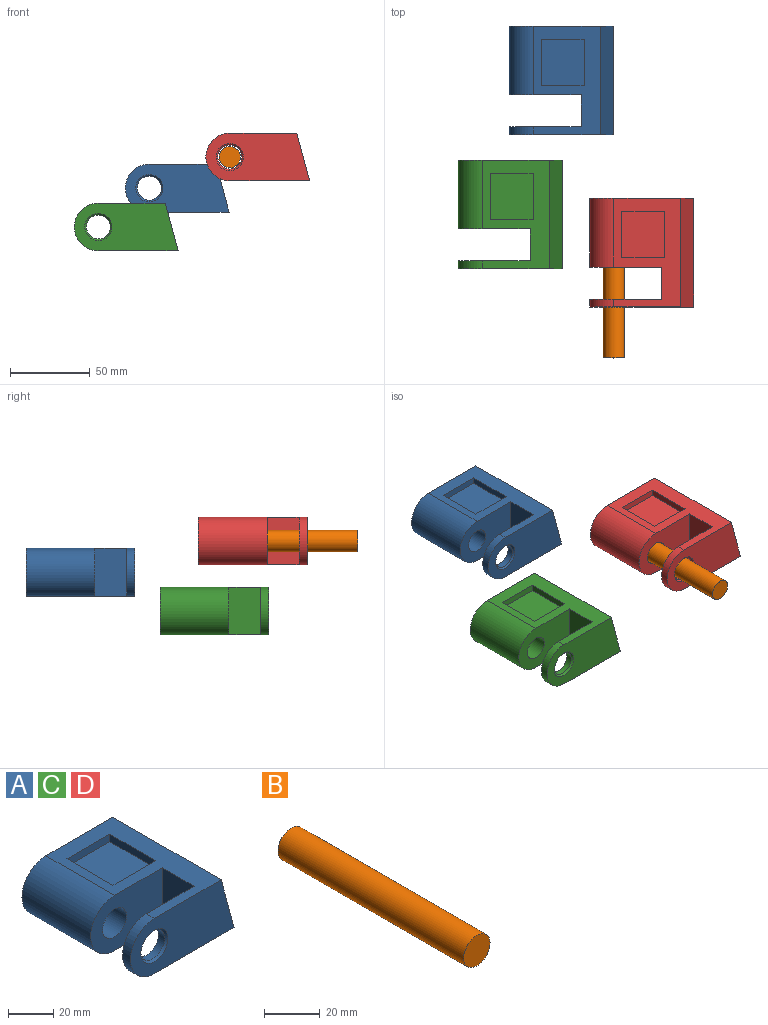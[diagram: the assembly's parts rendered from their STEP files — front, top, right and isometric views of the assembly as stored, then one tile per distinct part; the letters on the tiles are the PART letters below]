
ASSEMBLY  parts=4 mates=1
PART A: 19 faces, bbox 65x68.1x30 mm
  f0: plane 68.1x41.96mm, normal (0,0,1), area 1483.2mm2, adj f1,f2,f3,f5,f6,f7,f8,f9
  f1: cylinder r=15mm len=43.1mm, axis (0,1,0), area 2031mm2, adj f0,f4,f6,f9
  f2: plane 68.1x30mm, normal (0.97,0,0.26), area 2115.1mm2, adj f0,f4,f5,f6
  f3: cylinder r=15mm len=30mm, axis (0,1,0), area 235.6mm2, adj f0,f4,f5,f7
  f4: plane 68.1x50mm, normal (0,0,-1), area 2805mm2, adj f1,f2,f3,f5,f6,f7,f8,f9
  f5: plane 65x30mm, normal (0,-1,0), area 1505.9mm2, adj f0,f2,f3,f4,f12
  f6: plane 65x30mm, normal (0,1,0), area 1505.9mm2, adj f0,f1,f2,f4,f13
  f7: plane 45x30mm, normal (0,1,0), area 1076.7mm2, adj f0,f3,f4,f8,f11
  f8: plane 30x20mm, normal (-1,0,0), area 600mm2, adj f0,f4,f7,f9
  f9: plane 45x30mm, normal (0,-1,0), area 1076.7mm2, adj f0,f1,f4,f8,f10
  f10: cylinder r=7.5mm len=42.1mm, axis (0,1,0), area 1983.9mm2, adj f9,f13
  f11: cylinder r=7.5mm len=15mm, axis (0,1,0), area 188.5mm2, adj f7,f12
  f12: cone r=7.5mm half-angle=45deg, axis (0,-1,0), area 71.1mm2, adj f5,f11
  f13: cone r=7.5mm half-angle=45deg, axis (0,1,0), area 71.1mm2, adj f6,f10
  f14: plane 26.82x4.1mm, normal (0,1,0), area 110mm2, adj f0,f15,f17,f18
  f15: plane 28.87x4.1mm, normal (-1,0,0), area 118.4mm2, adj f0,f14,f16,f18
  f16: plane 26.82x4.1mm, normal (0,-1,0), area 110mm2, adj f0,f15,f17,f18
  f17: plane 28.87x4.1mm, normal (1,0,0), area 118.4mm2, adj f0,f14,f16,f18
  f18: plane 28.87x26.82mm, normal (0,0,1), area 774.4mm2, adj f14,f15,f16,f17
PART B: 3 faces, bbox 13.4x93.9x13.4 mm
  f0: cylinder r=6.69mm len=93.9mm, axis (0,1,0), area 3946.2mm2, adj f1,f2
  f1: plane 13.38x13.38mm, normal (0,-1,0), area 140.5mm2, adj f0
  f2: plane 13.38x13.38mm, normal (0,1,0), area 140.5mm2, adj f0
PART C: same geometry as A
PART D: same geometry as A
PLACE A t=(1.27,27.56,-1.87)mm
PLACE B rot(axis=(0,1,0),21.7deg) t=(51.73,-102.51,17.64)mm
PLACE C t=(-30.69,-56.48,-26.2)mm
PLACE D t=(51.73,-80.56,17.64)mm fixed
MATE revolute D.f1 <-> B.f0  axis (0,-1,0) through (51.73,-80.56,17.64)mm
